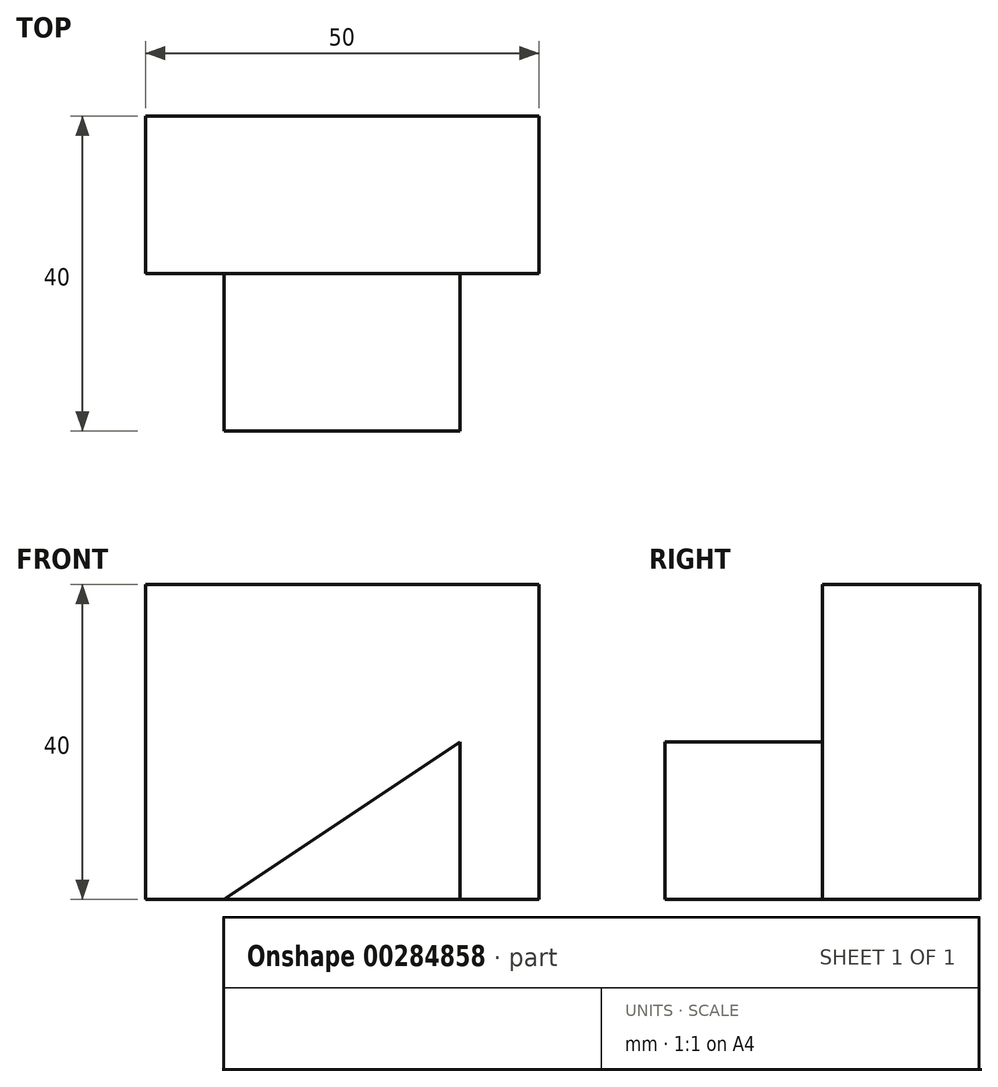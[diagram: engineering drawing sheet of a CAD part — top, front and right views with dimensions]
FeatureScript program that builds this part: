
annotation { "Feature Type Name" : "Feature", "Feature Type Description" : "" }
export const myFeature = defineFeature(function(context is Context, id is Id, definition is map)
    precondition{}
    {
        {
            var Q0;
            Q0=qCreatedBy(makeId("Front.planeOp"),FACE);
            var sketch = newSketch(context, id + "F0", { "sketchPlane" : qUnion([Q0])});
            skLineSegment(sketch, "E0.bottom", {"start": v(0, 0) * mm, "end": v(50, 0) * mm});
            skLineSegment(sketch, "E0.top", {"start": v(0, 40) * mm, "end": v(50, 40) * mm});
            skLineSegment(sketch, "E0.left", {"start": v(0, 0) * mm, "end": v(0, 40) * mm});
            skLineSegment(sketch, "E0.right", {"start": v(50, 0) * mm, "end": v(50, 40) * mm});
            skSolve(sketch);
        }
        {
            var Q0;
            Q0=qSketchRegion(id+"F0",true);
            extrude(context, id + "F1", {"entities" : qUnion([Q0]), "depth" : 20 * mm});
        }
        {
            var Q0;
            Q0=makeQuery(id+"F1.opExtrude","CAP_FACE",FACE,{"disambiguationData":[OSD([sQuery(id+"F0.wireOp",EDGE,"E0.bottom"),sQuery(id+"F0.wireOp",EDGE,"E0.top"),sQuery(id+"F0.wireOp",EDGE,"E0.left"),sQuery(id+"F0.wireOp",EDGE,"E0.right")])],"isStart":false});
            var sketch = newSketch(context, id + "F2", { "sketchPlane" : qUnion([Q0])});
            skLineSegment(sketch, "E1.bottom", {"start": v(10, 0) * mm, "end": v(40, 0) * mm});
            skLineSegment(sketch, "E1.top", {"start": v(10, 20) * mm, "end": v(40, 20) * mm});
            skLineSegment(sketch, "E1.left", {"start": v(10, 0) * mm, "end": v(10, 20) * mm});
            skLineSegment(sketch, "E1.right", {"start": v(40, 0) * mm, "end": v(40, 20) * mm});
            skLineSegment(sketch, "E2", {"start": v(40, 20) * mm, "end": v(10, 0) * mm});
            skSolve(sketch);
        }
        {
            var Q0;
            Q0=makeQuery(id+"F2.imprint","IMPRINT",FACE,{"disambiguationData":[TD([[makeQuery(id+"F2.imprint","IMPRINT",EDGE,{"derivedFrom":sQuery(id+"F2.wireOp",EDGE,"E1.bottom")}),1.0]])]});
            extrude(context, id + "F3", {"entities" : qUnion([Q0]), "operationType" : NewBodyOperationType.ADD, "depth" : 20 * mm});
        }
    });
